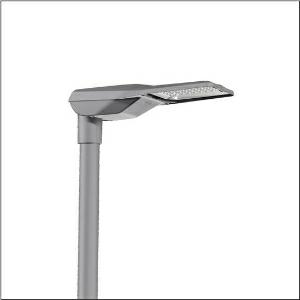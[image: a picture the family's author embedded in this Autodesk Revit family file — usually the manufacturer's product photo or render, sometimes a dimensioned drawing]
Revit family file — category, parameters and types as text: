
# Revit family: streetlight_sl_21_iq_mini___st1_0a_5xe2d41d08jb_acb7
name_source: partatom
category: Lighting Fixtures
units: mm (PartAtom-declared; Revit-internal decimal feet)

## family parameters
Cut with Voids When Loaded = No
Host = Face
Light Source = No
Part Type = Normal
Room Calculation Point = No
Round Connector Dimension = Use Diameter
Shared = No

## types (1)
- --- (1 x LED, 11290 lm, 71.6 W, 4000K)
    Apparent Load = 72 VA
    CIE Flux Codes = 40 73 97 100 100
    Color Rendering = 70
    Color Temperature = 4000K
    Default Elevation = 1800 mm
    Description = Streetlight SL 21 iQ mini, mast luminaire, primary light control with lens, of PMMA, primary optical cover: cover, of toughened safety glass, transparent, light distribution: ST1.0a, light emission: direct distribution, primary light characteristic: asymmetric, installation type: post-top, side-entry, LED, High Power LED, rated luminous flux: 11.290lm, luminous efficacy: 158lm/W, light colour: 740, colour temperature: 4000K, control gear: iQ-Comfort, control: Auto-Match, Temp-Guard, Lumen-Switch, Night-Set, Smart-Wire, Light-Fading, Desk-Remote (wireless, voltage-free reading and setting of iQ features in the workshop via application-optimized NFC function/RFID function), optimised constant luminous flux control (CLO 2.0), pre-setting: linear dimming characteristic, mains connection: 220..240V, AC, 50/60Hz, start of lifetime: 72W, end of service life: 75W, reduction: 33W, luminaire housing, of diecast aluminium, powder-coated, Siteco® metallic grey (DB 702S), corrosivity category C5 mid according to DIN EN ISO 12944, please order mast flange separately, inclination adjustable: 0°, 5°, 10°, 15°, sealing non-destructively replaceable, multi-level sealing system, length: 628mm, width: 235mm, height: 110mm, mast flange for spigot size: 42mm (side-entry): 5XC10008XM4, 60/48mm (side-entry/post-top): 5XC10108XM2, 76/60mm (side-entry/post-top): 5XC10108XM1, mounting height: 4..8m, protection rating (complete): IP66, insulation class (complete): insulation class II (safety insulation), certification: CE, ENEC, ENEC+, VDE, impact resistance: IK10, permissible operating ambient temperature for outdoor applications: -40..+50°C, standard-compliant lighting for roads and squares, packaging unit: 1 piece

Light Distribution: ST1.0a
    Height = 110 mm
    Lamp = 1 x LED
    Lamp Light Flux = 11290 lm
    Lamp Power = 71.6 W
    Lamp count = 1
    Length = 625 mm
    Luminous efficacy = 158 lm/W
    Manufacturer = Siteco
    ModVariant = No
    Model = 5XE2D41D08JB
    Number of Poles = 1
    OnlyDefault = Yes
    Power Factor = 1
    Product Name = Streetlight SL 21 iQ mini | ST1.0a
    Product group = mast luminaire | pylon top
    ProductGroupID = 6100
    Protection Class = Protection class II
    Protection Degree = IP 66
    RLX_Detail_Level = 1
    RLX_Emergency_Light_Flux = 0 lm
    RLX_Emergency_Type = 0
    RLX_Emergency_Type_DB = No
    RlxData = <blob elided: 26309 chars, md5=2de7cbd5>
    Socket = socket
    Standby Power = 0 W
    System Light Flux = 11290 lm
    System Power = 72 W
    Type Comments = factory setting: luminous flux: 100 % | dim-lin: 254 | 746 mA
    Type Image = l_1003519.jpg
    URL = http://relux.com
    VarID = @adj_171124
    Voltage = 0 V
    Weight = 0.00 kg
    Width = 234 mm

## geometry (parser evidence)
native form markers: Blend x4, Sweep x9
no freeform markers — native parametric forms only
